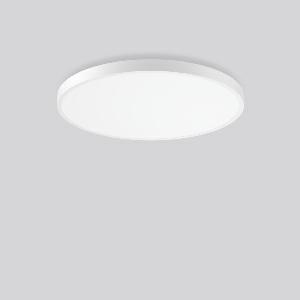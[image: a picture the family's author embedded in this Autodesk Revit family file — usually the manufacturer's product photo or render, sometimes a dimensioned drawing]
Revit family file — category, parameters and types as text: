
# Revit family: triona_round_a_312388_002_76_c63b
name_source: partatom
category: Lighting Fixtures
units: mm (PartAtom-declared; Revit-internal decimal feet)

## family parameters
Cut with Voids When Loaded = No
Host = Face
Light Source = No
Part Type = Normal
Room Calculation Point = No
Round Connector Dimension = Use Diameter
Shared = No

## types (1)
- TRIONA round A (1 x LED Modul 830, 12400 lm, 3000)
    Apparent Load = 133 VA
    CIE Flux Codes = 49 80 96 71 100
    Color Rendering = 80
    Color Temperature = 3000
    Default Elevation = 1800 mm
    Description = Series: TRIONA round
Decorative round LED surface-mounted luminaire. Flat, seamless frame: aluminium extrusion profile, powder coated. Cover made of sheet steel, powder-coated. Direct light emission through a diffuser plastic opal. Indirect light emission through a flush diffuser made of satin-finish plastic. Lightguide and diffuser made of non-yellowing plastic (PMMA). Lateral light emission (RZB SIDELITE technology) for above-average homogeneous light distribution. Direct 70%, indirect 30% light emission. Suitable for Ceiling mounting, Wall (surface). Tool-free mounting via bayonet connection. Electronic ballast included. Very easy installation thanks to Plug+Play connection. 
Colour: traffic white, matt (RAL 9016)
Diameter: 845 mm
Height: 88 mm
Lamp: LED
Socket: without socket
Colour temperature: 3000K
Colour rendering index (CRI): 80
System power: 133 W
Rated luminous flux: 12400 lm
Luminous efficiency: 93 lm/W
Control gear: Converter, dimmable, DALI
Protection class: I
Type of protection: IP 20
    Height = 88 mm
    Lamp = 1 x LED Modul 830
    Lamp Light Flux = 12400 lm
    Lamp count = 1
    Length = 845 mm
    Lifetime = 50000 h
    Luminous efficacy = 93 lm/W
    Manufacturer = RZB
    ModVariant = No
    Model = 312388.002.76
    Mounting Place = Ceiling
    Mounting Type = Surface mounted
    Number of Poles = 1
    OnlyDefault = Yes
    Power Factor = 1
    Product Name = TRIONA round A
    Product group = Surface mounted modular luminaires
    ProductGroupID = 306
    Protection Class = Protection class I
    Protection Degree = IP 20
    RLX_Detail_Level = 1
    RLX_Emergency_Light_Flux = 0 lm
    RLX_Emergency_Type = 0
    RLX_Emergency_Type_DB = No
    RlxData = <blob elided: 40973 chars, md5=54b834cd>
    Socket = socket
    Standby Power = 0 W
    System Light Flux = 12400 lm
    System Power = 133 W
    Type Comments = Product without accessories
    Type Image = 312388.002.jpg
    URL = http://relux.com
    VarID = ---
    Voltage = 230 V
    Voltage Range = 220-240 V
    Weight = 0.00 kg
    Width = 0 mm  [stored 0 ft]

note: [stored X ft] marks values corroborated as IEEE doubles in the binary element streams (Revit-internal decimal feet)

## geometry (parser evidence)
native form markers: Blend x4, Sweep x14
no freeform markers — native parametric forms only
